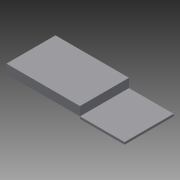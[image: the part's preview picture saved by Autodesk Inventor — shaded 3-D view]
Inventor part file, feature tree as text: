
AUTODESK INVENTOR PART (.ipt)
format: ipt  version: 2014 SP1 (Build 180222100, 222)  size: 78,848 bytes
history: native  units: in
note: dims shown in document units (in); Inventor stores cm internally (conversion verified against a paired STEP export)
features: extrude x2, sketch x2
ambient origin geometry x8: Origin, YZ Plane, XZ Plane, XY Plane, X Axis, Y Axis, Z Axis, Center Point
bodies: Solid1 (feature_tree)
feature tree (4):
  extrude  "Extrusion1"  Depth=4.0in
  extrude  "Extrusion2"  Depth=22.0in
  sketch  "Sketch1"  dims[d0=33.0in d1=4.0in]
  sketch  "Sketch2"  dims[d2=22.0in d3=0.0in d4=22.0in d5=1.0in d6=20.0in d7=0.0in]
